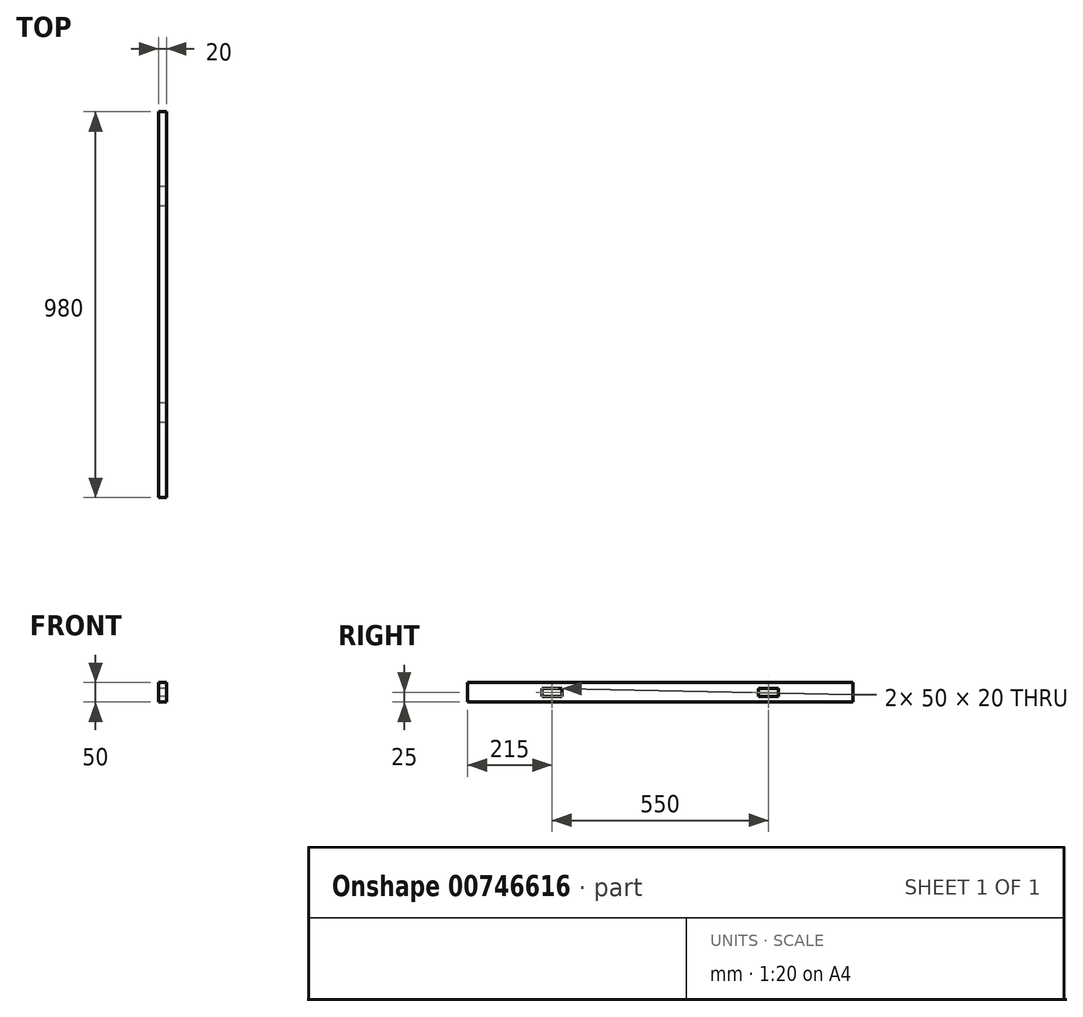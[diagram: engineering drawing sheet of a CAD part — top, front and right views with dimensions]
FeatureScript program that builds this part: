
annotation { "Feature Type Name" : "Feature", "Feature Type Description" : "" }
export const myFeature = defineFeature(function(context is Context, id is Id, definition is map)
    precondition{}
    {
        {
            var Q0;
            Q0=qCreatedBy(makeId("Front.planeOp"),FACE);
            var sketch = newSketch(context, id + "F0", { "sketchPlane" : qUnion([Q0])});
            skLineSegment(sketch, "E0.bottom", {"start": v(10, -25) * mm, "end": v(-10, -25) * mm});
            skLineSegment(sketch, "E0.top", {"start": v(10, 25) * mm, "end": v(-10, 25) * mm});
            skLineSegment(sketch, "E0.left", {"start": v(10, -25) * mm, "end": v(10, 25) * mm});
            skLineSegment(sketch, "E0.right", {"start": v(-10, -25) * mm, "end": v(-10, 25) * mm});
            skPoint(sketch, "E0.middle", {"position": v(0, 0) * mm});
            skSolve(sketch);
        }
        {
            var Q0;
            Q0=makeQuery(id+"F0.imprint","IMPRINT",FACE,{"disambiguationData":[TD([[makeQuery(id+"F0.imprint","IMPRINT",EDGE,{"derivedFrom":sQuery(id+"F0.wireOp",EDGE,"E0.bottom")}),-1.0]])]});
            extrude(context, id + "F1", {"entities" : qUnion([Q0]), "oppositeDirection" : true, "depth" : 980 * mm, "offsetDistance" : 25 * mm});
        }
        {
            var Q0;
            Q0=makeQuery(id+"F1.opExtrude","SWEPT_FACE",FACE,{"disambiguationData":[OSD([sQuery(id+"F0.wireOp",EDGE,"E0.right")])]});
            var sketch = newSketch(context, id + "F2", { "sketchPlane" : qUnion([Q0])});
            skLineSegment(sketch, "E1.bottom", {"start": v(-740, -10) * mm, "end": v(-790, -10) * mm});
            skLineSegment(sketch, "E1.top", {"start": v(-740, 10) * mm, "end": v(-790, 10) * mm});
            skLineSegment(sketch, "E1.left", {"start": v(-740, -10) * mm, "end": v(-740, 10) * mm});
            skLineSegment(sketch, "E1.right", {"start": v(-790, -10) * mm, "end": v(-790, 10) * mm});
            skPoint(sketch, "E1.middle", {"position": v(-765, 0) * mm});
            skLineSegment(sketch, "E2.bottom", {"start": v(-240, 10) * mm, "end": v(-190, 10) * mm});
            skLineSegment(sketch, "E2.top", {"start": v(-240, -10) * mm, "end": v(-190, -10) * mm});
            skLineSegment(sketch, "E2.left", {"start": v(-240, 10) * mm, "end": v(-240, -10) * mm});
            skLineSegment(sketch, "E2.right", {"start": v(-190, 10) * mm, "end": v(-190, -10) * mm});
            skPoint(sketch, "E2.middle", {"position": v(-215, 0) * mm});
            skSolve(sketch);
        }
        {
            var Q0;
            Q0 = qSketchRegion(id + "F2", true);
            extrude(context, id + "F3", {"entities" : qUnion([Q0]), "operationType" : NewBodyOperationType.REMOVE, "endBound" : BoundingType.THROUGH_ALL, "oppositeDirection" : true, "depth" : 25 * mm, "offsetDistance" : 25 * mm});
        }
    });
